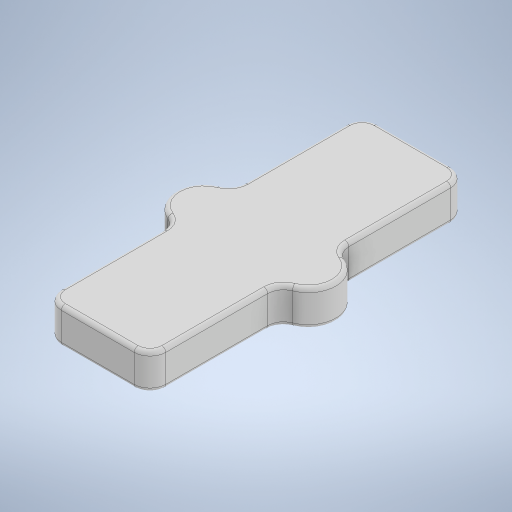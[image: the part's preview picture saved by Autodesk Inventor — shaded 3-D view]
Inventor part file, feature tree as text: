
AUTODESK INVENTOR PART (.ipt)
format: ipt  version: 2023 (Build 270158000, 158)  size: 310,272 bytes
history: native  units: mm
features: extrude x3, sketch x2, fillet x2, chamfer x1
ambient origin geometry x8: Origin, YZ Plane, XZ Plane, XY Plane, X Axis, Y Axis, Z Axis, Center Point
bodies: Solid1 (feature_tree)
feature tree (8):
  extrude  "Extrusion1"  Depth=40.0mm
  sketch  "Sketch2"  dims[d2=4.5mm d3=0.0mm d4=4.1mm d5=7.0mm d6=4.5mm d7=0.0mm d8=3.1mm d9=0.0mm d10=2.0mm d11=0.5mm d12=0.25mm d13=2.0mm d14=45.0deg]
  extrude  "Extrusion2"  Depth=2.0mm
  extrude  "Extrusion3"  Depth=2.0mm
  fillet  "Fillet1"  Radius=4.5mm
  fillet  "Fillet2"  Radius=3.1mm
  chamfer  "Chamfer1"  Distance=2.0mm
  sketch  "Sketch1"  dims[d0=13.2mm d1=40.0mm]
